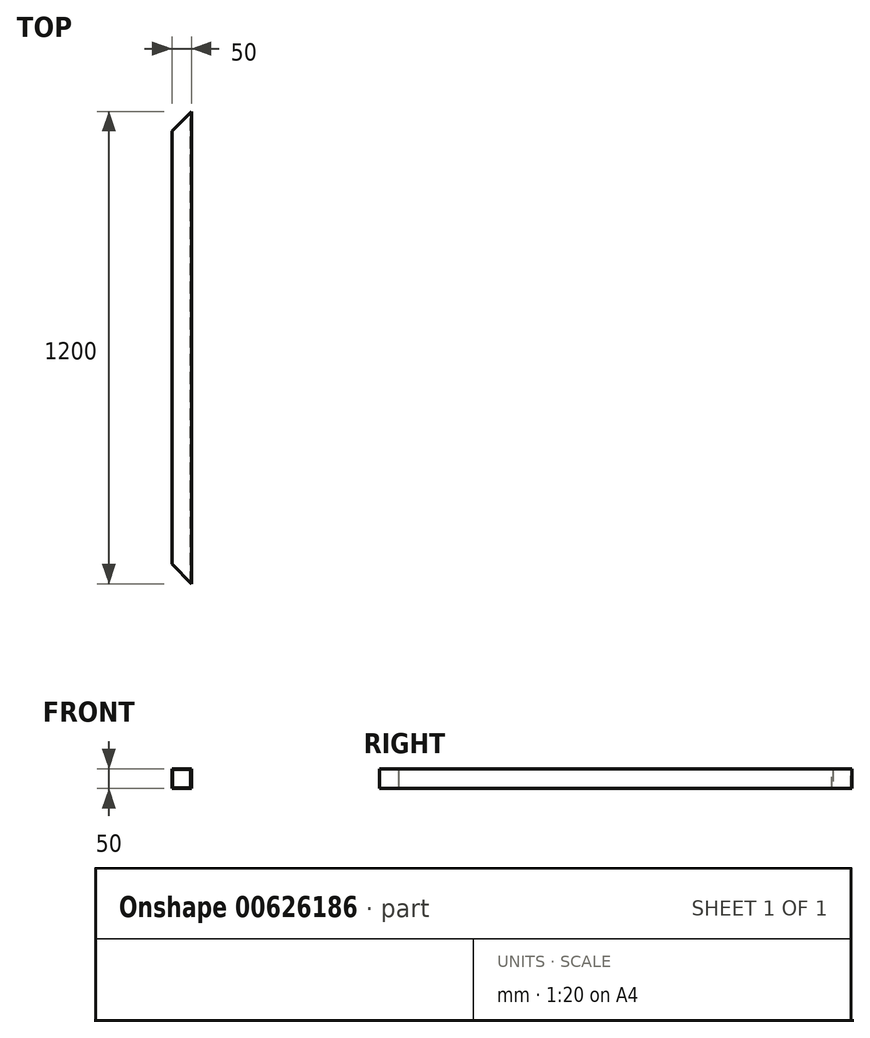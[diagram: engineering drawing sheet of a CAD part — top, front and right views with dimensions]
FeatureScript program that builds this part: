
annotation { "Feature Type Name" : "Feature", "Feature Type Description" : "" }
export const myFeature = defineFeature(function(context is Context, id is Id, definition is map)
    precondition{}
    {
        {
            var Q0;
            Q0=qCreatedBy(makeId("Front.planeOp"),FACE);
            var sketch = newSketch(context, id + "F0", { "sketchPlane" : qUnion([Q0])});
            skLineSegment(sketch, "E0", {"start": v(0, 0) * mm, "end": v(50, 0) * mm});
            skLineSegment(sketch, "E1", {"start": v(50, 0) * mm, "end": v(50, 50) * mm});
            skLineSegment(sketch, "E2", {"start": v(50, 50) * mm, "end": v(0, 50) * mm});
            skLineSegment(sketch, "E3", {"start": v(0, 50) * mm, "end": v(0, 0) * mm});
            skLineSegment(sketch, "E4.0", {"start": v(48, 48) * mm, "end": v(2, 48) * mm});
            skLineSegment(sketch, "E5.0", {"start": v(48, 2) * mm, "end": v(48, 48) * mm});
            skLineSegment(sketch, "E6.0", {"start": v(2, 48) * mm, "end": v(2, 2) * mm});
            skLineSegment(sketch, "E7.0", {"start": v(2, 2) * mm, "end": v(48, 2) * mm});
            skSolve(sketch);
        }
        {
            var Q0;
            {var subQ0=sQuery(id+"F0.wireOp",EDGE,"E2");Q0=makeQuery(id+"F0.imprint","IMPRINT",FACE,{"disambiguationData":[TD([[makeQuery(id+"F0.imprint","IMPRINT",EDGE,{"derivedFrom":subQ0}),1.0]])]});}
            extrude(context, id + "F1", {"entities" : qUnion([Q0]), "depth" : 1200 * mm, "offsetDistance" : 25 * mm});
        }
        {
            var Q0;
            Q0=makeQuery(id+"F1.opExtrude","SWEPT_FACE",FACE,{"disambiguationData":[OSD([sQuery(id+"F0.wireOp",EDGE,"E2")])]});
            var sketch = newSketch(context, id + "F2", { "sketchPlane" : qUnion([Q0])});
            skLineSegment(sketch, "E8", {"start": v(0, 0) * mm, "end": v(0, -50) * mm});
            skLineSegment(sketch, "E9", {"start": v(0, -50) * mm, "end": v(50, 0) * mm});
            skLineSegment(sketch, "E10", {"start": v(50, 0) * mm, "end": v(0, 0) * mm});
            skLineSegment(sketch, "E11", {"start": v(0, -1200) * mm, "end": v(0, -1150) * mm});
            skLineSegment(sketch, "E12", {"start": v(0, -1150) * mm, "end": v(50, -1200) * mm});
            skLineSegment(sketch, "E13", {"start": v(50, -1200) * mm, "end": v(0, -1200) * mm});
            skSolve(sketch);
        }
        {
            var Q0;
            Q0=makeQuery(id+"F2.imprint","IMPRINT",FACE,{"disambiguationData":[TD([[makeQuery(id+"F2.imprint","IMPRINT",EDGE,{"derivedFrom":sQuery(id+"F2.wireOp",EDGE,"E8")}),-1.0]])]});
            extrude(context, id + "F3", {"entities" : qUnion([Q0]), "operationType" : NewBodyOperationType.REMOVE, "oppositeDirection" : true, "depth" : 50 * mm, "offsetDistance" : 25 * mm});
        }
        {
            var Q0;
            Q0 = qSketchRegion(id + "F2", true);
            extrude(context, id + "F4", {"entities" : qUnion([Q0]), "operationType" : NewBodyOperationType.REMOVE, "oppositeDirection" : true, "depth" : 50 * mm, "offsetDistance" : 25 * mm});
        }
    });
